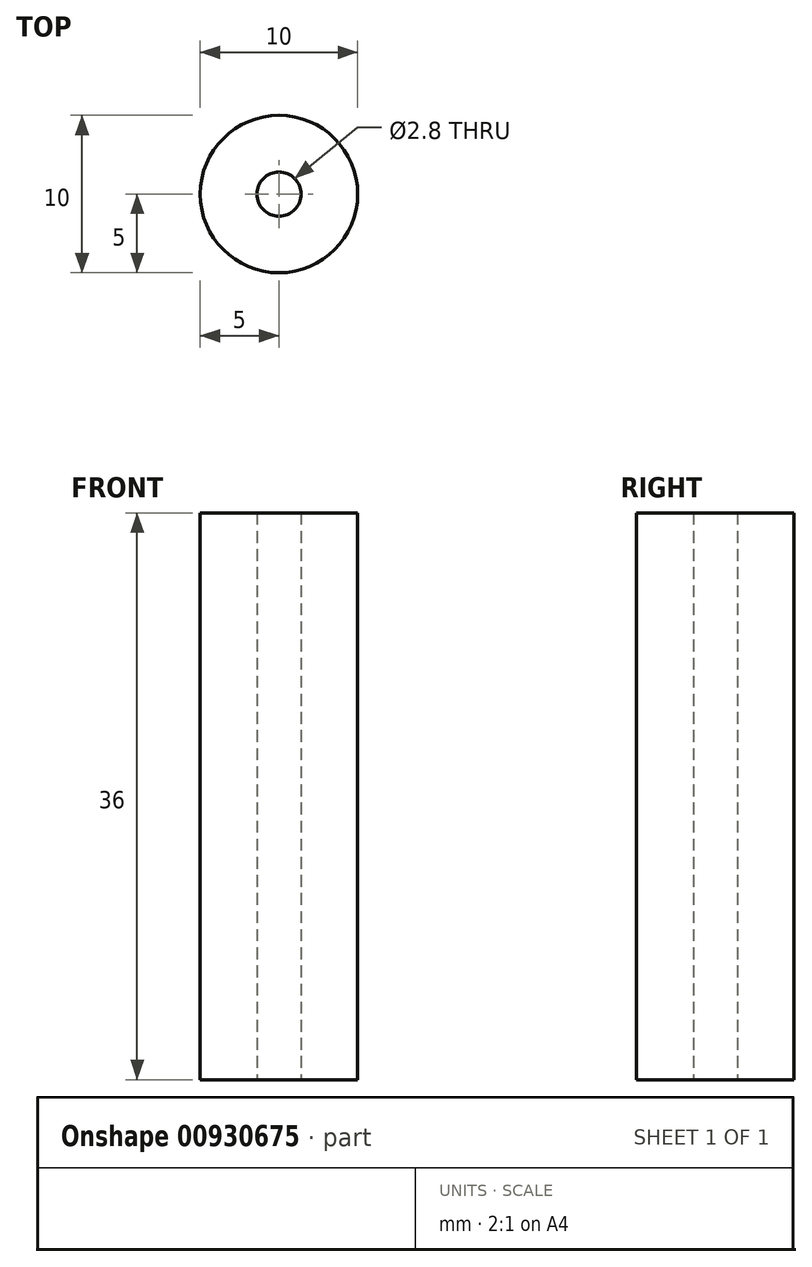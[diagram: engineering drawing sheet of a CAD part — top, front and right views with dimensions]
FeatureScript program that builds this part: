
annotation { "Feature Type Name" : "Feature", "Feature Type Description" : "" }
export const myFeature = defineFeature(function(context is Context, id is Id, definition is map)
    precondition{}
    {
        {
            var Q0;
            Q0=qCreatedBy(makeId("Top.planeOp"),FACE);
            var sketch = newSketch(context, id + "F0", { "sketchPlane" : qUnion([Q0])});
            skCircle(sketch, "E0", {"center": v(0, 0) * mm, "radius": 5 * mm});
            skCircle(sketch, "E1", {"center": v(0, 0) * mm, "radius": 1.4 * mm});
            skSolve(sketch);
        }
        {
            var Q0;
            Q0=qSketchRegion(id+"F0",true);
            extrude(context, id + "F1", {"entities" : qUnion([Q0]), "depth" : 36 * mm});
        }
    });
